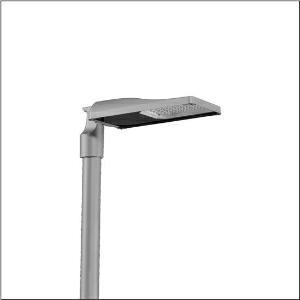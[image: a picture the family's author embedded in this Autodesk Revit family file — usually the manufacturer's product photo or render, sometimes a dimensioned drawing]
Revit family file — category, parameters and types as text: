
# Revit family: streetlight_sl_31_mini___st1_0a_5xh6d31b08ja_158d
name_source: partatom
category: Lighting Fixtures
units: mm (PartAtom-declared; Revit-internal decimal feet)

## family parameters
Cut with Voids When Loaded = No
Host = Face
Light Source = No
Part Type = Normal
Room Calculation Point = No
Round Connector Dimension = Use Diameter
Shared = No

## types (1)
- --- (1 x LED, 12140 lm, 81.1 W, 3000K)
    Apparent Load = 81 VA
    CIE Flux Codes = 40 73 97 100 100
    Color Rendering = 70
    Color Temperature = 3000K
    Default Elevation = 1800 mm
    Description = Streetlight SL 31 mini, mast luminaire, primary light control with lens, of PMMA, primary optical cover: cover, of toughened safety glass, transparent, light distribution: ST1.0a, light emission: direct distribution, primary light characteristic: asymmetric, installation type: post-top, side-entry, LED, High Power LED, rated luminous flux: 12.140lm, luminous efficacy: 150lm/W, light colour: 730, colour temperature: 3000K, control: presetting dimming linear, flexible luminous flux parameterisation, time-dependent luminous flux control, constant luminous flux control, power reduction, intelligent temperature release in ECG and LED module, overheat protection, with cable H07RN-F 3x 1.5mm², mains connection: 220..240V, AC, 50/60Hz, connection cable pre-assembled, cable length: 10,5m, start of lifetime: 81W, end of service life: 88W, reduction: 36W, luminaire housing, of diecast aluminium, powder-coated, Siteco® metallic grey (DB 702S), corrosivity category C5 high according to DIN EN ISO 12944, no sealing on luminaire upper side, inclination: -15°..+20° (post-top) | -20°..+20° (side-entry), adjustable in 5° steps, mast flange (76/60mm) included as standard, multi-level sealing system, sealing non-destructively replaceable, protection rating (complete): IP66, insulation class (complete): insulation class II (safety insulation), certification: CE, ENEC, ENEC+, VDE, UKCA, impact resistance: IK09, permissible operating ambient temperature for outdoor applications: -40..+50°C, standard-compliant lighting for roads and squares, packaging unit: 1 piece

Light Distribution: ST1.0a
    Height = 76 mm
    Lamp = 1 x LED
    Lamp Light Flux = 12140 lm
    Lamp Power = 81.1 W
    Lamp count = 1
    Length = 547 mm
    Luminous efficacy = 150 lm/W
    Manufacturer = Siteco
    ModVariant = No
    Model = 5XH6D31B08JA
    Number of Poles = 1
    OnlyDefault = Yes
    Power Factor = 1
    Product Name = Streetlight SL 31 mini | ST1.0a
    Product group = mast luminaire | pylon top
    ProductGroupID = 6100
    Protection Class = Protection class II
    Protection Degree = IP 66
    RLX_Detail_Level = 1
    RLX_Emergency_Light_Flux = 0 lm
    RLX_Emergency_Type = 0
    RLX_Emergency_Type_DB = No
    RlxData = <blob elided: 39973 chars, md5=250c2f9f>
    Socket = socket
    Standby Power = 0 W
    System Light Flux = 12140 lm
    System Power = 81 W
    Type Comments = factory setting: luminous flux: 100 % | dim-lin: 254 | 860 mA
    Type Image = l_1300326.jpg
    URL = http://relux.com
    VarID = @adj_008055
    Voltage = 0 V
    Weight = 0.00 kg
    Width = 265 mm

## geometry (parser evidence)
native form markers: Blend x4, Sweep x9
no freeform markers — native parametric forms only
